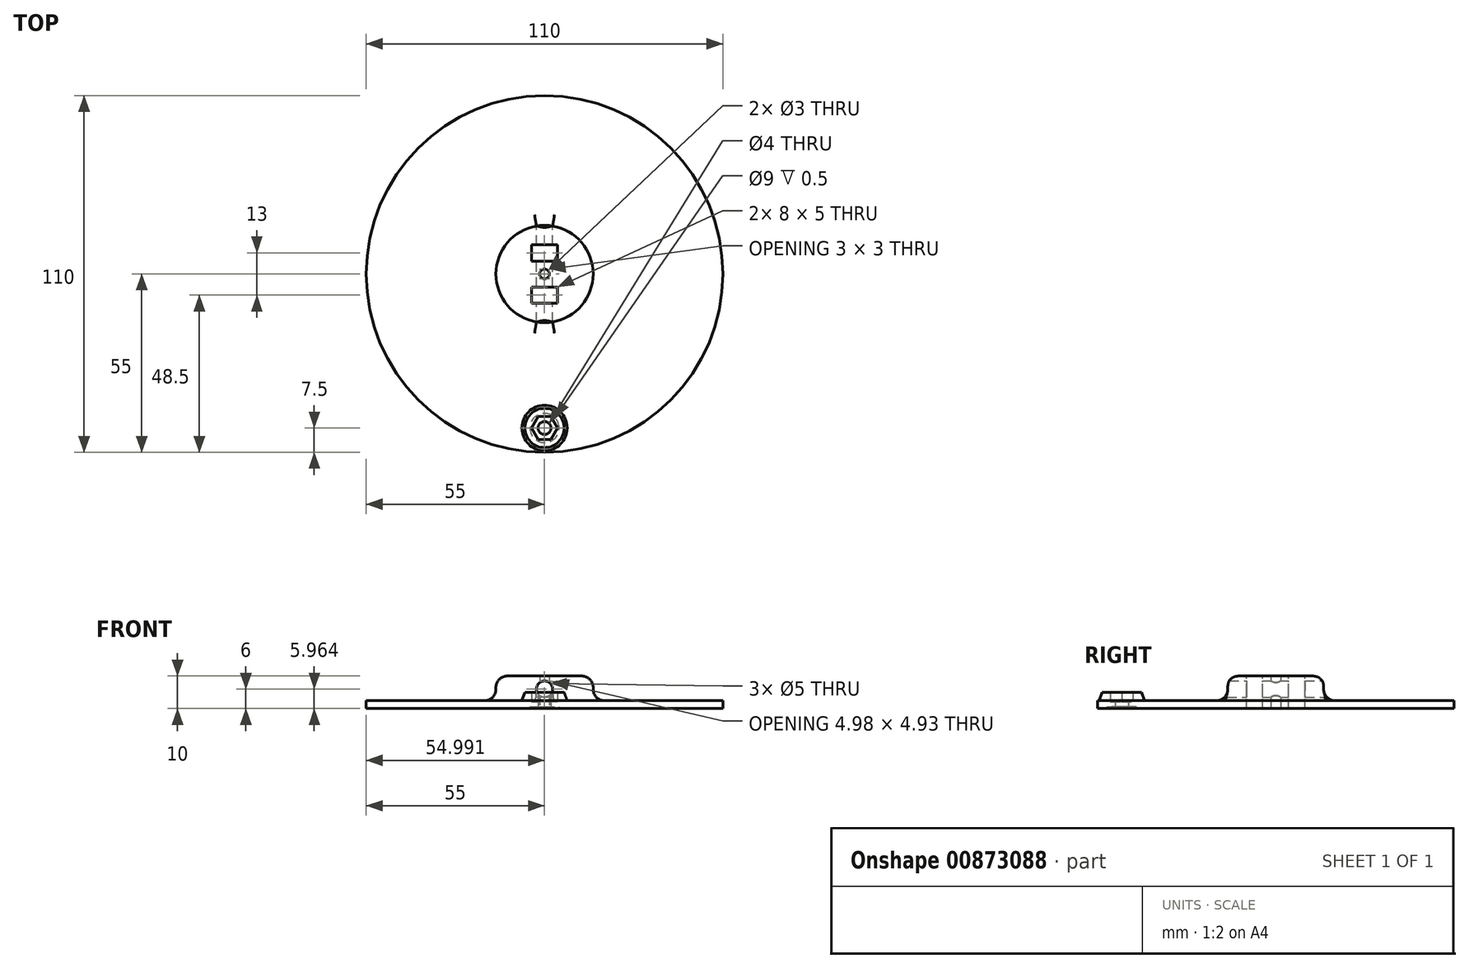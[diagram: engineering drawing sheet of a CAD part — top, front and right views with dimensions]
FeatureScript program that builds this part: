
annotation { "Feature Type Name" : "Feature", "Feature Type Description" : "" }
export const myFeature = defineFeature(function(context is Context, id is Id, definition is map)
    precondition{}
    {
        {
            var Q0;
            Q0=qCreatedBy(makeId("Top.planeOp"),FACE);
            var sketch = newSketch(context, id + "F0", { "sketchPlane" : qUnion([Q0])});
            skCircle(sketch, "E0", {"center": v(0, 0) * mm, "radius": 55 * mm});
            skSolve(sketch);
        }
        {
            var Q0;
            Q0 = qSketchRegion(id + "F0", true);
            extrude(context, id + "F1", {"entities" : qUnion([Q0]), "depth" : 2.4 * mm, "offsetDistance" : 25 * mm});
        }
        {
            var Q0;
            Q0=qCreatedBy(makeId("Top.planeOp"),FACE);
            var sketch = newSketch(context, id + "F2", { "sketchPlane" : qUnion([Q0])});
            skCircle(sketch, "E1", {"center": v(0, 0) * mm, "radius": 15 * mm});
            skSolve(sketch);
        }
        {
            var Q0;
            Q0=makeQuery(id+"F2.imprint","IMPRINT",FACE,{"disambiguationData":[TD([[makeQuery(id+"F2.imprint","IMPRINT",EDGE,{"derivedFrom":sQuery(id+"F2.wireOp",EDGE,"E1")}),1.0]])]});
            extrude(context, id + "F3", {"entities" : qUnion([Q0]), "operationType" : NewBodyOperationType.ADD, "depth" : 10 * mm, "offsetDistance" : 25 * mm});
        }
        {
            var Q0;
            Q0=qCreatedBy(makeId("Top.planeOp"),FACE);
            var sketch = newSketch(context, id + "F4", { "sketchPlane" : qUnion([Q0])});
            skCircle(sketch, "E2", {"center": v(0, 0) * mm, "radius": 1.5 * mm});
            skSolve(sketch);
        }
        {
            var Q0;
            Q0 = qSketchRegion(id + "F4", true);
            extrude(context, id + "F5", {"entities" : qUnion([Q0]), "operationType" : NewBodyOperationType.REMOVE, "depth" : 25 * mm, "offsetDistance" : 25 * mm});
        }
        {
            var Q0;
            Q0=makeQuery(id+"F3.opExtrude","CAP_FACE",FACE,{"disambiguationData":[OSD([sQuery(id+"F2.wireOp",EDGE,"E1")])],"isStart":false});
            var sketch = newSketch(context, id + "F6", { "sketchPlane" : qUnion([Q0])});
            skLineSegment(sketch, "E3.bottom", {"start": v(-4, 9) * mm, "end": v(4, 9) * mm});
            skLineSegment(sketch, "E3.top", {"start": v(-4, 4) * mm, "end": v(4, 4) * mm});
            skLineSegment(sketch, "E3.left", {"start": v(-4, 9) * mm, "end": v(-4, 4) * mm});
            skLineSegment(sketch, "E3.right", {"start": v(4, 9) * mm, "end": v(4, 4) * mm});
            skLineSegment(sketch, "E4.bottom", {"start": v(-4, -4) * mm, "end": v(4, -4) * mm});
            skLineSegment(sketch, "E4.top", {"start": v(-4, -9) * mm, "end": v(4, -9) * mm});
            skLineSegment(sketch, "E4.left", {"start": v(-4, -4) * mm, "end": v(-4, -9) * mm});
            skLineSegment(sketch, "E4.right", {"start": v(4, -4) * mm, "end": v(4, -9) * mm});
            skSolve(sketch);
        }
        {
            var Q0;
            Q0 = qSketchRegion(id + "F6", true);
            extrude(context, id + "F7", {"entities" : qUnion([Q0]), "operationType" : NewBodyOperationType.REMOVE, "oppositeDirection" : true, "depth" : 12 * mm, "offsetDistance" : 25 * mm});
        }
        {
            var Q0;
            Q0=makeQuery(id+"F7.boolean.opBoolean","COPY",FACE,{"derivedFrom":makeQuery(id+"F7.opExtrude","SWEPT_FACE",FACE,{"disambiguationData":[OSD([sQuery(id+"F6.wireOp",EDGE,"E3.bottom")])]})});
            var sketch = newSketch(context, id + "F8", { "sketchPlane" : qUnion([Q0])});
            skCircle(sketch, "E5", {"center": v(0, 6) * mm, "radius": 2.5 * mm});
            skSolve(sketch);
        }
        {
            var Q0;
            Q0 = qSketchRegion(id + "F8", true);
            var Q1;
            Q1=makeQuery(id+"F3.opExtrude","SWEPT_FACE",FACE,{"disambiguationData":[OSD([sQuery(id+"F2.wireOp",EDGE,"E1")])]});
            var Q2;
            Q2=makeQuery(id+"F3.opExtrude","SWEPT_FACE",FACE,{"disambiguationData":[OSD([sQuery(id+"F2.wireOp",EDGE,"E1")])]});
            extrude(context, id + "F9", {"entities" : qUnion([Q0]), "operationType" : NewBodyOperationType.REMOVE, "endBound" : BoundingType.UP_TO_SURFACE, "depth" : 25 * mm, "endBoundEntityFace" : qUnion([Q1]), "offsetDistance" : 25 * mm, "hasSecondDirection" : true, "secondDirectionBound" : SecondDirectionBoundingType.UP_TO_SURFACE, "secondDirectionOppositeDirection" : true, "secondDirectionDepth" : 25 * mm, "secondDirectionBoundEntityFace" : qUnion([Q2])});
        }
        {
            var Q0;
            Q0=qCreatedBy(makeId("Top.planeOp"),FACE);
            var sketch = newSketch(context, id + "F10", { "sketchPlane" : qUnion([Q0])});
            skCircle(sketch, "E6", {"center": v(0, 0) * mm, "radius": 47.5 * mm, "construction": true});
            skSolve(sketch);
        }
        {
            var Q0;
            Q0=qCreatedBy(makeId("Top.planeOp"),FACE);
            var Q1;
            Q1=qCreatedBy(makeId("Top.planeOp"),FACE);
            var Q2;
            Q2=qCreatedBy(makeId("Top.planeOp"),FACE);
            var sketch = newSketch(context, id + "F11", { "sketchPlane" : qUnion([Q0, Q1, Q2])});
            skCircle(sketch, "E7", {"center": v(0, -47.5) * mm, "radius": 5 * mm});
            skSolve(sketch);
        }
        {
            var Q0;
            Q0 = qSketchRegion(id + "F11", true);
            extrude(context, id + "F12", {"entities" : qUnion([Q0]), "operationType" : NewBodyOperationType.ADD, "depth" : 5 * mm, "offsetDistance" : 25 * mm});
        }
        {
            var Q0;
            Q0=makeQuery(id+"F1.opExtrude","CAP_FACE",FACE,{"disambiguationData":[OSD([sQuery(id+"F0.wireOp",EDGE,"E0")])],"isStart":true});
            var sketch = newSketch(context, id + "F13", { "sketchPlane" : qUnion([Q0])});
            skCircle(sketch, "E8", {"center": v(0, 47.5) * mm, "radius": 4.5 * mm});
            skSolve(sketch);
        }
        {
            var Q0;
            Q0 = qSketchRegion(id + "F13", true);
            extrude(context, id + "F14", {"entities" : qUnion([Q0]), "operationType" : NewBodyOperationType.REMOVE, "oppositeDirection" : true, "depth" : 0.5 * mm, "offsetDistance" : 25 * mm});
        }
        {
            var Q0;
            Q0=qCreatedBy(makeId("Top.planeOp"),FACE);
            var sketch = newSketch(context, id + "F15", { "sketchPlane" : qUnion([Q0])});
            skCircle(sketch, "E9", {"center": v(0, -47.5) * mm, "radius": 2 * mm});
            skSolve(sketch);
        }
        {
            var Q0;
            Q0 = qSketchRegion(id + "F15", true);
            extrude(context, id + "F16", {"entities" : qUnion([Q0]), "operationType" : NewBodyOperationType.REMOVE, "depth" : 25 * mm, "offsetDistance" : 25 * mm});
        }
        {
            var Q0;
            Q0=qCreatedBy(makeId("Top.planeOp"),FACE);
            var sketch = newSketch(context, id + "F17", { "sketchPlane" : qUnion([Q0])});
            skCircle(sketch, "E10.cCircle", {"center": v(0, -47.5) * mm, "radius": 3.5 * mm, "construction": true});
            skLineSegment(sketch, "E10.0", {"start": v(-2.02, -44) * mm, "end": v(2.02, -44) * mm});
            skLineSegment(sketch, "E10.1", {"start": v(2.02, -44) * mm, "end": v(4.04, -47.5) * mm});
            skLineSegment(sketch, "E10.2", {"start": v(4.04, -47.5) * mm, "end": v(2.02, -51) * mm});
            skLineSegment(sketch, "E10.3", {"start": v(2.02, -51) * mm, "end": v(-2.02, -51) * mm});
            skLineSegment(sketch, "E10.4", {"start": v(-2.02, -51) * mm, "end": v(-4.04, -47.5) * mm});
            skLineSegment(sketch, "E10.5", {"start": v(-4.04, -47.5) * mm, "end": v(-2.02, -44) * mm});
            skPoint(sketch, "E10.0.midPoint", {"position": v(0, -44) * mm});
            skSolve(sketch);
        }
        {
            var Q0;
            Q0 = qSketchRegion(id + "F17", true);
            var Q1;
            Q1=makeQuery(id+"F12.opExtrude","CAP_FACE",FACE,{"disambiguationData":[OSD([sQuery(id+"F11.wireOp",EDGE,"E7")])],"isStart":false});
            var Q2;
            Q2=makeQuery(id+"F12.opExtrude","CAP_FACE",FACE,{"disambiguationData":[OSD([sQuery(id+"F11.wireOp",EDGE,"E7")])],"isStart":false});
            extrude(context, id + "F18", {"entities" : qUnion([Q0]), "operationType" : NewBodyOperationType.REMOVE, "endBound" : BoundingType.UP_TO_SURFACE, "depth" : -2 * mm, "endBoundEntityFace" : qUnion([Q1]), "offsetDistance" : 1.5 * mm, "offsetOppositeDirection" : true, "hasSecondDirection" : true, "secondDirectionOppositeDirection" : false, "secondDirectionDepth" : 2 * mm, "secondDirectionBoundEntityFace" : qUnion([Q2])});
        }
        {
            var Q0;
            Q0=makeQuery(id+"F12.boolean.opBoolean","INTERSECT",EDGE,{"derivedFrom":[makeQuery(id+"F1.opExtrude","CAP_FACE",FACE,{"disambiguationData":[OSD([sQuery(id+"F0.wireOp",EDGE,"E0")])],"isStart":false}),makeQuery(id+"F12.opExtrude","SWEPT_FACE",FACE,{"disambiguationData":[OSD([sQuery(id+"F11.wireOp",EDGE,"E7")])]})]});
            chamfer(context, id + "F19", {"entities" : qUnion([Q0]), "chamferType" : ChamferType.TWO_OFFSETS, "width1" : 2 * mm, "oppositeDirection" : false, "width2" : 5.5 * mm, "tangentPropagation" : true});
        }
        {
            var Q0;
            Q0=makeQuery(id+"F3.boolean.opBoolean","INTERSECT",EDGE,{"derivedFrom":[makeQuery(id+"F1.opExtrude","CAP_FACE",FACE,{"disambiguationData":[OSD([sQuery(id+"F0.wireOp",EDGE,"E0")])],"isStart":false}),makeQuery(id+"F3.opExtrude","SWEPT_FACE",FACE,{"disambiguationData":[OSD([sQuery(id+"F2.wireOp",EDGE,"E1")])]})]});
            var Q1;
            Q1=makeQuery(id+"F3.opExtrude","CAP_EDGE",EDGE,{"disambiguationData":[OSD([sQuery(id+"F2.wireOp",EDGE,"E1")])],"isStart":false});
            fillet(context, id + "F20", {"entities" : qUnion([Q0, Q1]), "radius" : 3.5 * mm, "tangentPropagation" : true, "allowEdgeOverflow" : false});
        }
    });
